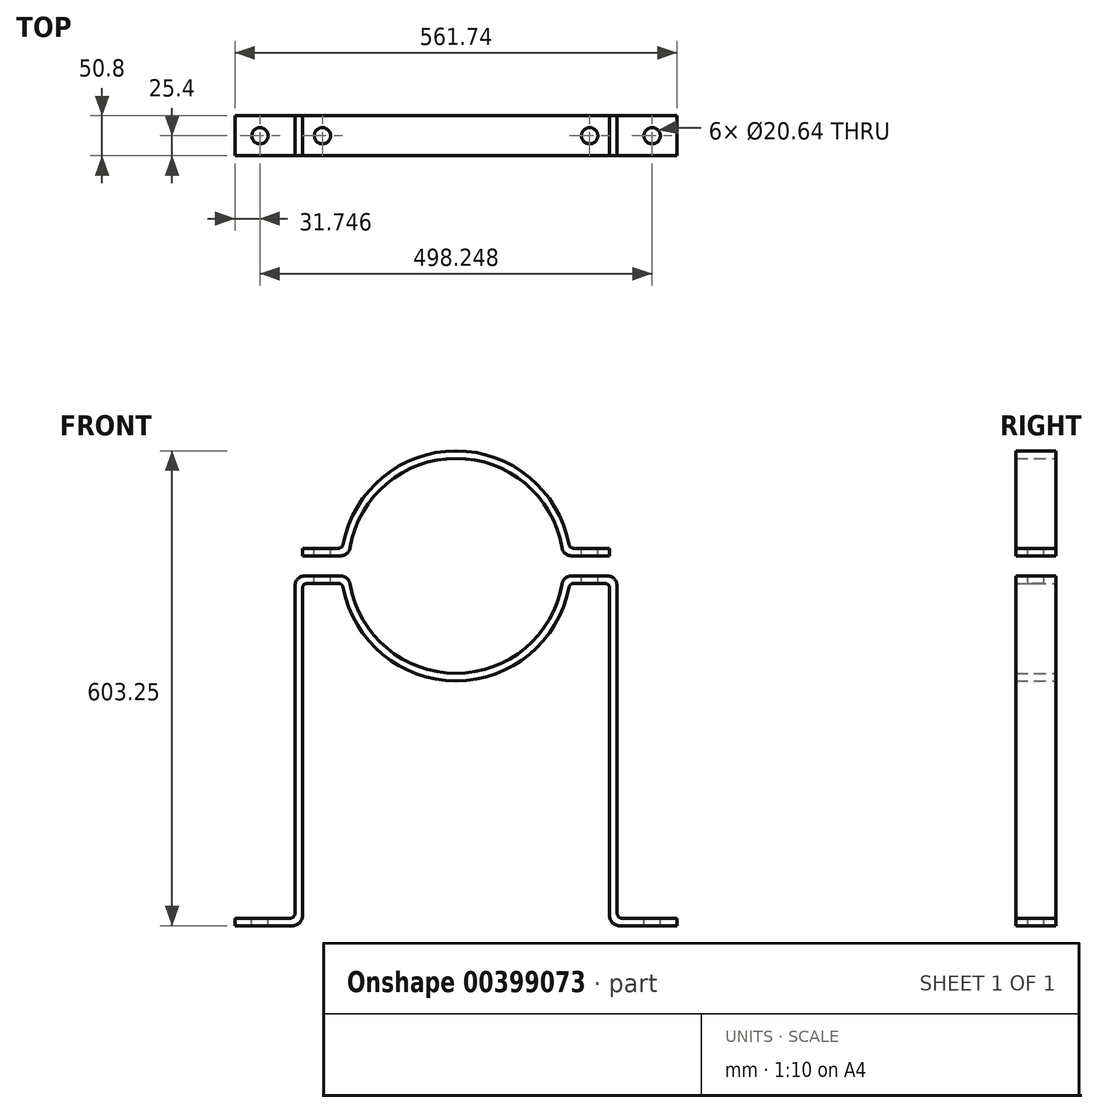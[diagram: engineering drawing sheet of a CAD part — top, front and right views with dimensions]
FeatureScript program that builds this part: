
annotation { "Feature Type Name" : "Feature", "Feature Type Description" : "" }
export const myFeature = defineFeature(function(context is Context, id is Id, definition is map)
    precondition{}
    {
        {
            var Q0;
            Q0=qCreatedBy(makeId("Front.planeOp"),FACE);
            var sketch = newSketch(context, id + "F0", { "sketchPlane" : qUnion([Q0])});
            skArc(sketch, "E0", {"start": v(-135.93, -12.7) * mm, "mid": v(0, -136.53) * mm, "end": v(135.93, -12.7) * mm});
            skArc(sketch, "E1", {"start": v(-144.35, -22.23) * mm, "mid": v(0, -146.05) * mm, "end": v(144.35, -22.23) * mm});
            skLineSegment(sketch, "E2.bottom", {"start": v(195.15, 22.23) * mm, "end": v(144.35, 22.23) * mm});
            skLineSegment(sketch, "E2.top", {"start": v(195.15, 12.7) * mm, "end": v(135.93, 12.7) * mm});
            skPoint(sketch, "E2.middle", {"position": v(0, 17.46) * mm});
            skLineSegment(sketch, "E3.MirrorCS", {"start": v(195.15, -12.7) * mm, "end": v(145.5, -12.7) * mm});
            skLineSegment(sketch, "E4.MirrorCS", {"start": v(195.15, -22.23) * mm, "end": v(144.35, -22.23) * mm});
            skLineSegment(sketch, "E5", {"start": v(0, 0) * mm, "end": v(0, -146.05) * mm});
            skPoint(sketch, "E5.endSnap0", {"position": v(0, -12.7) * mm});
            skLineSegment(sketch, "E6", {"start": v(-195.15, -457.2) * mm, "end": v(-280.87, -457.2) * mm});
            skLineSegment(sketch, "E7", {"start": v(195.15, -457.2) * mm, "end": v(280.87, -457.2) * mm});
            skLineSegment(sketch, "E8", {"start": v(-195.15, -22.22) * mm, "end": v(-195.15, -457.2) * mm});
            skLineSegment(sketch, "E9", {"start": v(-280.87, -447.68) * mm, "end": v(-204.67, -447.68) * mm});
            skLineSegment(sketch, "E10", {"start": v(-204.67, -447.68) * mm, "end": v(-204.67, -12.7) * mm});
            skLineSegment(sketch, "E11", {"start": v(-204.67, -12.7) * mm, "end": v(-195.15, -12.7) * mm});
            skLineSegment(sketch, "E12.MirrorCS", {"start": v(195.15, -22.22) * mm, "end": v(195.15, -457.2) * mm});
            skLineSegment(sketch, "E13.MirrorCS", {"start": v(204.67, -447.67) * mm, "end": v(204.67, -12.7) * mm});
            skLineSegment(sketch, "E14.MirrorCS", {"start": v(204.67, -12.7) * mm, "end": v(195.15, -12.7) * mm});
            skLineSegment(sketch, "E15.MirrorCS", {"start": v(280.87, -447.67) * mm, "end": v(204.67, -447.68) * mm});
            skLineSegment(sketch, "E16.trimOffspring", {"start": v(-144.35, 22.22) * mm, "end": v(-195.15, 22.22) * mm});
            skLineSegment(sketch, "E17.trimOffspring", {"start": v(-144.35, -22.22) * mm, "end": v(-195.15, -22.22) * mm});
            skPoint(sketch, "E18.MirrorCS.start.orphan", {"position": v(-195.15, -22.23) * mm});
            skLineSegment(sketch, "E19.trimOffspring", {"start": v(-135.93, -12.7) * mm, "end": v(-195.15, -12.7) * mm});
            skLineSegment(sketch, "E20.trimOffspring", {"start": v(-135.93, 12.7) * mm, "end": v(-195.15, 12.7) * mm});
            skArc(sketch, "E21.trimOffspring", {"start": v(144.35, 22.23) * mm, "mid": v(0, 146.05) * mm, "end": v(-144.35, 22.23) * mm});
            skArc(sketch, "E22.trimOffspring", {"start": v(135.93, 12.7) * mm, "mid": v(0, 136.53) * mm, "end": v(-135.93, 12.7) * mm});
            skLineSegment(sketch, "E23", {"start": v(145.5, -12.7) * mm, "end": v(135.93, -12.7) * mm});
            skPoint(sketch, "E24.MirrorCS.end.orphan", {"position": v(195.15, -12.7) * mm});
            skPoint(sketch, "E24.MirrorCS.start.orphan", {"position": v(195.15, -22.22) * mm});
            skPoint(sketch, "E25.MirrorCS.start.orphan", {"position": v(195.15, -22.23) * mm});
            skPoint(sketch, "E26.orphan", {"position": v(0, -457.2) * mm});
            skPoint(sketch, "E27.orphan", {"position": v(-558.8, -457.2) * mm});
            skPoint(sketch, "E28.trimOffspring.end.orphan", {"position": v(558.8, -457.2) * mm});
            skLineSegment(sketch, "E29", {"start": v(-195.15, 22.22) * mm, "end": v(-195.15, 12.7) * mm});
            skLineSegment(sketch, "E30.MirrorCS", {"start": v(195.15, 22.22) * mm, "end": v(195.15, 12.7) * mm});
            skPoint(sketch, "E31.orphan", {"position": v(195.15, 22.23) * mm});
            skPoint(sketch, "E32.orphan", {"position": v(195.15, 12.7) * mm});
            skPoint(sketch, "E2.right.end.orphan", {"position": v(-195.15, 12.7) * mm});
            skPoint(sketch, "E2.right.start.orphan", {"position": v(-195.15, 22.23) * mm});
            skPoint(sketch, "E33.orphan", {"position": v(-195.15, -12.7) * mm});
            skLineSegment(sketch, "E34", {"start": v(-280.87, -447.68) * mm, "end": v(-280.87, -457.2) * mm});
            skLineSegment(sketch, "E35.MirrorCS", {"start": v(280.87, -447.68) * mm, "end": v(280.87, -457.2) * mm});
            skPoint(sketch, "E36.end.orphan", {"position": v(-306.27, -447.68) * mm});
            skPoint(sketch, "E36.start.orphan", {"position": v(-306.27, -457.2) * mm});
            skPoint(sketch, "E37.orphan", {"position": v(306.27, -447.67) * mm});
            skPoint(sketch, "E38.orphan", {"position": v(306.27, -457.2) * mm});
            skSolve(sketch);
        }
        {
            var Q0;
            Q0 = qSketchRegion(id + "F0", true);
            extrude(context, id + "F1", {"entities" : qUnion([Q0]), "endBound" : BoundingType.SYMMETRIC, "depth" : 50.8 * mm});
        }
        {
            var Q0;
            Q0=makeQuery(id+"F1.opExtrude","SWEPT_FACE",FACE,{"disambiguationData":[OSD([sQuery(id+"F0.wireOp",EDGE,"E2.bottom")])]});
            var sketch = newSketch(context, id + "F2", { "sketchPlane" : qUnion([Q0])});
            skCircle(sketch, "E39", {"center": v(-169.75, 0) * mm, "radius": 10.32 * mm});
            skCircle(sketch, "E40.MirrorC", {"center": v(169.75, 0) * mm, "radius": 10.32 * mm});
            skSolve(sketch);
        }
        {
            var Q0;
            Q0 = qSketchRegion(id + "F2", true);
            extrude(context, id + "F3", {"entities" : qUnion([Q0]), "operationType" : NewBodyOperationType.REMOVE, "endBound" : BoundingType.THROUGH_ALL, "oppositeDirection" : true, "depth" : 50.8 * mm});
        }
        {
            var Q0;
            Q0=makeQuery(id+"F1.opExtrude","SWEPT_FACE",FACE,{"disambiguationData":[OSD([sQuery(id+"F0.wireOp",EDGE,"E15.MirrorCS")])]});
            var sketch = newSketch(context, id + "F4", { "sketchPlane" : qUnion([Q0])});
            skCircle(sketch, "E41", {"center": v(-249.12, 0) * mm, "radius": 10.32 * mm});
            skCircle(sketch, "E42.MirrorC", {"center": v(249.12, 0) * mm, "radius": 10.32 * mm});
            skSolve(sketch);
        }
        {
            var Q0;
            Q0 = qSketchRegion(id + "F4", true);
            extrude(context, id + "F5", {"entities" : qUnion([Q0]), "operationType" : NewBodyOperationType.REMOVE, "oppositeDirection" : true, "depth" : 25.4 * mm});
        }
        {
            var Q0;
            Q0=makeQuery(id+"F1.opExtrude","SWEPT_EDGE",EDGE,{"disambiguationData":[OSD([sQuery(id+"F0.wireOp",EDGE,"E10"),sQuery(id+"F0.wireOp",EDGE,"E11")])]});
            var Q1;
            Q1=makeQuery(id+"F1.opExtrude","SWEPT_EDGE",EDGE,{"disambiguationData":[OSD([sQuery(id+"F0.wireOp",EDGE,"E0"),sQuery(id+"F0.wireOp",EDGE,"E19.trimOffspring")])]});
            var Q2;
            Q2=makeQuery(id+"F1.opExtrude","SWEPT_EDGE",EDGE,{"disambiguationData":[OSD([sQuery(id+"F0.wireOp",EDGE,"E20.trimOffspring"),sQuery(id+"F0.wireOp",EDGE,"E22.trimOffspring")])]});
            var Q3;
            Q3=makeQuery(id+"F1.opExtrude","SWEPT_EDGE",EDGE,{"disambiguationData":[OSD([sQuery(id+"F0.wireOp",EDGE,"E0"),sQuery(id+"F0.wireOp",EDGE,"E23")])]});
            var Q4;
            Q4=makeQuery(id+"F1.opExtrude","SWEPT_EDGE",EDGE,{"disambiguationData":[OSD([sQuery(id+"F0.wireOp",EDGE,"E2.top"),sQuery(id+"F0.wireOp",EDGE,"E22.trimOffspring")])]});
            var Q5;
            Q5=makeQuery(id+"F1.opExtrude","SWEPT_EDGE",EDGE,{"disambiguationData":[OSD([sQuery(id+"F0.wireOp",EDGE,"E13.MirrorCS"),sQuery(id+"F0.wireOp",EDGE,"E14.MirrorCS")])]});
            fillet(context, id + "F6", {"entities" : qUnion([Q0, Q1, Q2, Q3, Q4, Q5]), "radius" : 12.7 * mm, "tangentPropagation" : true, "allowEdgeOverflow" : false});
        }
        {
            var Q0;
            Q0=makeQuery(id+"F1.opExtrude","SWEPT_EDGE",EDGE,{"disambiguationData":[OSD([sQuery(id+"F0.wireOp",EDGE,"E16.trimOffspring"),sQuery(id+"F0.wireOp",EDGE,"E21.trimOffspring")])]});
            var Q1;
            Q1=makeQuery(id+"F1.opExtrude","SWEPT_EDGE",EDGE,{"disambiguationData":[OSD([sQuery(id+"F0.wireOp",EDGE,"E1"),sQuery(id+"F0.wireOp",EDGE,"E17.trimOffspring")])]});
            var Q2;
            Q2=makeQuery(id+"F1.opExtrude","SWEPT_EDGE",EDGE,{"disambiguationData":[OSD([sQuery(id+"F0.wireOp",EDGE,"E8"),sQuery(id+"F0.wireOp",EDGE,"E17.trimOffspring")])]});
            var Q3;
            Q3=makeQuery(id+"F1.opExtrude","SWEPT_EDGE",EDGE,{"disambiguationData":[OSD([sQuery(id+"F0.wireOp",EDGE,"E1"),sQuery(id+"F0.wireOp",EDGE,"E4.MirrorCS")])]});
            var Q4;
            Q4=makeQuery(id+"F1.opExtrude","SWEPT_EDGE",EDGE,{"disambiguationData":[OSD([sQuery(id+"F0.wireOp",EDGE,"E4.MirrorCS"),sQuery(id+"F0.wireOp",EDGE,"E12.MirrorCS")])]});
            var Q5;
            Q5=makeQuery(id+"F1.opExtrude","SWEPT_EDGE",EDGE,{"disambiguationData":[OSD([sQuery(id+"F0.wireOp",EDGE,"E2.bottom"),sQuery(id+"F0.wireOp",EDGE,"E21.trimOffspring")])]});
            fillet(context, id + "F7", {"entities" : qUnion([Q0, Q1, Q2, Q3, Q4, Q5]), "radius" : 6.35 * mm, "tangentPropagation" : true, "allowEdgeOverflow" : false});
        }
        {
            var Q0;
            Q0=makeQuery(id+"F1.opExtrude","SWEPT_EDGE",EDGE,{"disambiguationData":[OSD([sQuery(id+"F0.wireOp",EDGE,"E8"),sQuery(id+"F0.wireOp",EDGE,"E6")])]});
            var Q1;
            Q1=makeQuery(id+"F1.opExtrude","SWEPT_EDGE",EDGE,{"disambiguationData":[OSD([sQuery(id+"F0.wireOp",EDGE,"E12.MirrorCS"),sQuery(id+"F0.wireOp",EDGE,"E7")])]});
            fillet(context, id + "F8", {"entities" : qUnion([Q0, Q1]), "radius" : 12.7 * mm, "tangentPropagation" : true, "allowEdgeOverflow" : false});
        }
        {
            var Q0;
            Q0=makeQuery(id+"F1.opExtrude","SWEPT_EDGE",EDGE,{"disambiguationData":[OSD([sQuery(id+"F0.wireOp",EDGE,"E13.MirrorCS"),sQuery(id+"F0.wireOp",EDGE,"E15.MirrorCS")])]});
            var Q1;
            Q1=makeQuery(id+"F1.opExtrude","SWEPT_EDGE",EDGE,{"disambiguationData":[OSD([sQuery(id+"F0.wireOp",EDGE,"E9"),sQuery(id+"F0.wireOp",EDGE,"E10")])]});
            fillet(context, id + "F9", {"entities" : qUnion([Q0, Q1]), "radius" : 6.35 * mm, "tangentPropagation" : true, "allowEdgeOverflow" : false});
        }
    });
